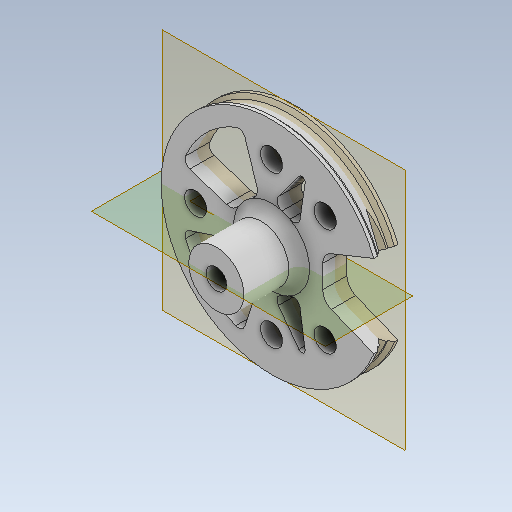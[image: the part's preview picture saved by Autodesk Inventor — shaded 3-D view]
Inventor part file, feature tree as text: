
AUTODESK INVENTOR PART (.ipt)
format: ipt  version: 2020 (Build 240168000, 168)  size: 314,368 bytes
history: native  units: mm
features: sketch x17, plane x4, other x3
ambient origin geometry x8: Origin, YZ Plane, XZ Plane, XY Plane, X Axis, Y Axis, Z Axis, Center Point
bodies: Solid1 (feature_tree)
feature tree (24):
  other  "tendon_wh_3.ipt"
  other  "Solid1::tendon_wh_3.ipt"
  other  "TaggingFeature1"
  sketch  "Sketch1"  dims[d0=10.0mm]
  sketch  "Sketch2"
  sketch  "Sketch3"
  sketch  "Sketch4"
  sketch  "Sketch5"
  sketch  "Sketch6"
  sketch  "Sketch7"
  sketch  "Sketch8"
  sketch  "Sketch9"
  sketch  "Sketch10"
  sketch  "Sketch11"
  sketch  "Sketch12"
  sketch  "Sketch13"
  sketch  "Sketch14"
  sketch  "Sketch15"
  sketch  "Sketch16"
  sketch  "Sketch17"
  plane  "Work Plane1"
  plane  "Work Plane2"
  plane  "Work Plane3"
  plane  "Work Plane4"
